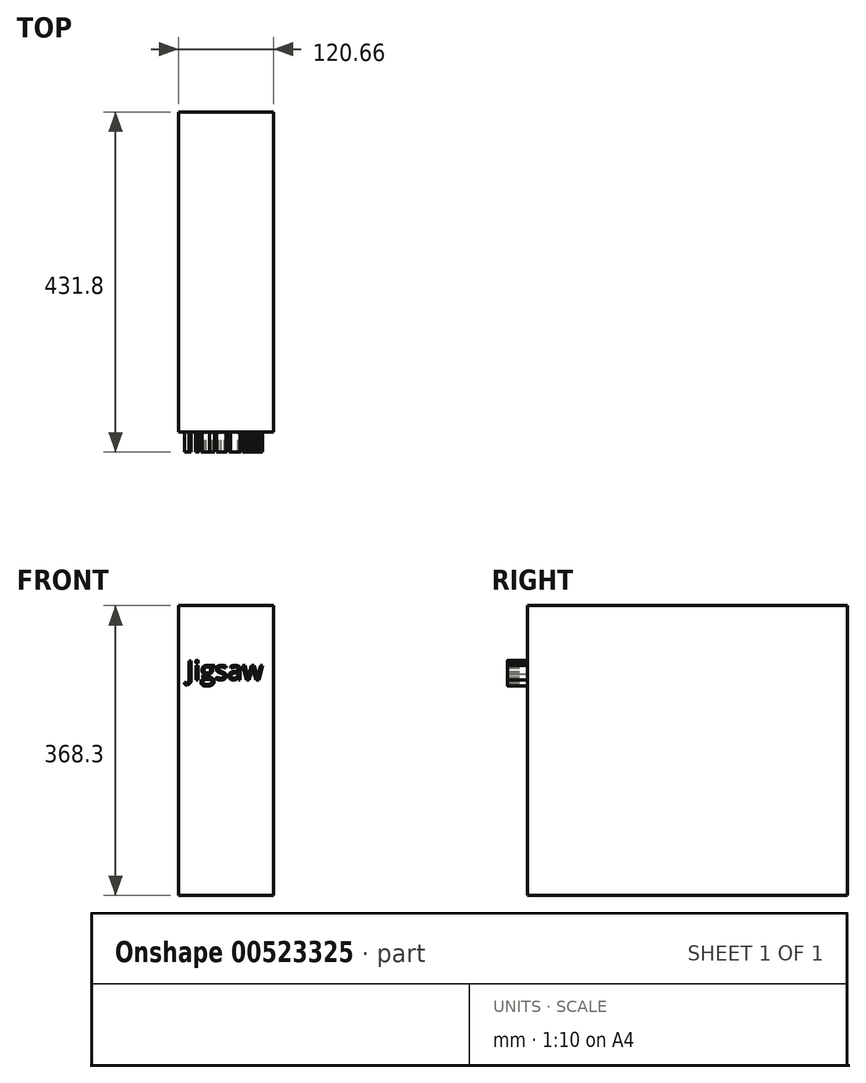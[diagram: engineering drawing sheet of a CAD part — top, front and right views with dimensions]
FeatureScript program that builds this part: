
annotation { "Feature Type Name" : "Feature", "Feature Type Description" : "" }
export const myFeature = defineFeature(function(context is Context, id is Id, definition is map)
    precondition{}
    {
        {
            var Q0;
            Q0=qCreatedBy(makeId("Front.planeOp"),FACE);
            var sketch = newSketch(context, id + "F0", { "sketchPlane" : qUnion([Q0])});
            skLineSegment(sketch, "E0.bottom", {"start": v(60.32, 184.15) * mm, "end": v(-60.33, 184.15) * mm});
            skLineSegment(sketch, "E0.top", {"start": v(60.32, -184.15) * mm, "end": v(-60.33, -184.15) * mm});
            skLineSegment(sketch, "E0.left", {"start": v(60.32, 184.15) * mm, "end": v(60.32, -184.15) * mm});
            skLineSegment(sketch, "E0.right", {"start": v(-60.33, 184.15) * mm, "end": v(-60.33, -184.15) * mm});
            skPoint(sketch, "E0.middle", {"position": v(0, 0) * mm});
            skSolve(sketch);
        }
        {
            var Q0;
            Q0=makeQuery(id+"F0.imprint","IMPRINT",FACE,{"disambiguationData":[TD([[makeQuery(id+"F0.imprint","IMPRINT",EDGE,{"derivedFrom":sQuery(id+"F0.wireOp",EDGE,"E0.bottom")}),1.0]])]});
            extrude(context, id + "F1", {"entities" : qUnion([Q0]), "depth" : 406.4 * mm, "offsetDistance" : 25.4 * mm});
        }
        {
            var Q0;
            Q0=makeQuery(id+"F1.opExtrude","CAP_FACE",FACE,{"disambiguationData":[OSD([sQuery(id+"F0.wireOp",EDGE,"E0.bottom"),sQuery(id+"F0.wireOp",EDGE,"E0.top"),sQuery(id+"F0.wireOp",EDGE,"E0.left"),sQuery(id+"F0.wireOp",EDGE,"E0.right")])],"isStart":false});
            var sketch = newSketch(context, id + "F2", { "sketchPlane" : qUnion([Q0])});
            skText(sketch, "E1", { "text": "Jigsaw", "fontName": "OpenSans-Regular.ttf"});
            const initialGuessF2  = {"E1": [-0.05018, 0.08987, 1, 0, 0.0243]};
            skSetInitialGuess(sketch, initialGuessF2);
            skSolve(sketch);
        }
        {
            var Q0;
            Q0 = qSketchRegion(id + "F2", true);
            extrude(context, id + "F3", {"entities" : qUnion([Q0]), "operationType" : NewBodyOperationType.ADD, "depth" : 25.4 * mm, "offsetDistance" : 25.4 * mm});
        }
    });
